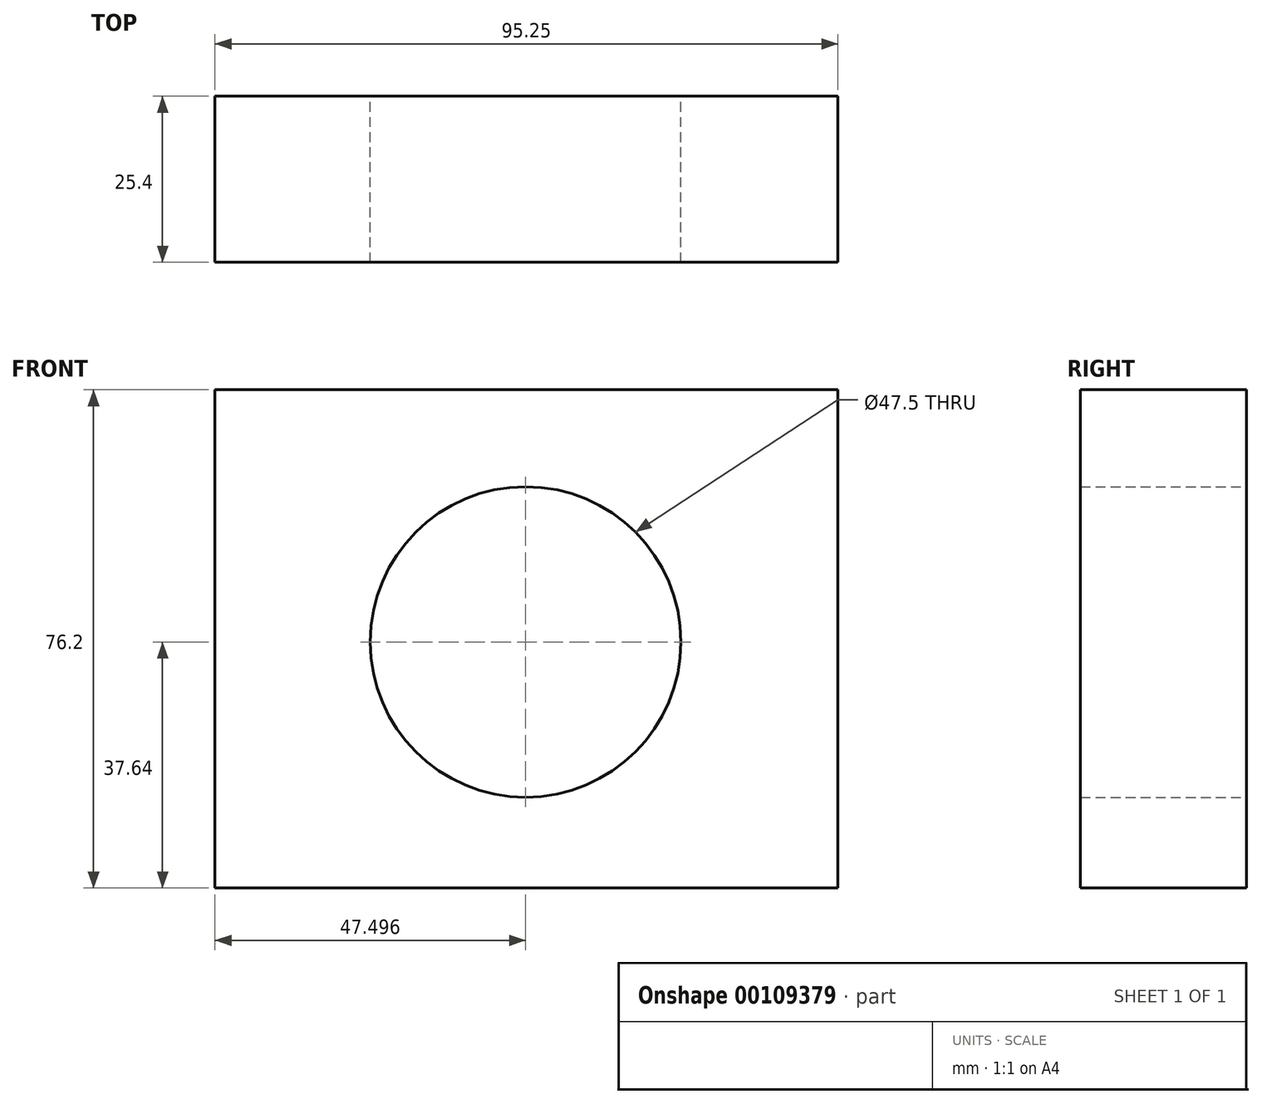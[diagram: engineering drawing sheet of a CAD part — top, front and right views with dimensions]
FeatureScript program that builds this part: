
annotation { "Feature Type Name" : "Feature", "Feature Type Description" : "" }
export const myFeature = defineFeature(function(context is Context, id is Id, definition is map)
    precondition{}
    {
        {
            var Q0;
            Q0=qCreatedBy(makeId("Front.planeOp"),FACE);
            var sketch = newSketch(context, id + "F0", { "sketchPlane" : qUnion([Q0])});
            skLineSegment(sketch, "E0", {"start": v(-36.86, 38.56) * mm, "end": v(-36.86, -37.64) * mm});
            skLineSegment(sketch, "E1", {"start": v(-36.86, -37.64) * mm, "end": v(58.39, -37.64) * mm});
            skLineSegment(sketch, "E2", {"start": v(58.39, -37.64) * mm, "end": v(58.39, 38.56) * mm});
            skLineSegment(sketch, "E3", {"start": v(58.39, 38.56) * mm, "end": v(-36.86, 38.56) * mm});
            skLineSegment(sketch, "E4", {"start": v(58.39, 0.46) * mm, "end": v(10.64, 0) * mm, "construction": true});
            skCircle(sketch, "E5", {"center": v(10.64, 0) * mm, "radius": 23.75 * mm});
            skSolve(sketch);
        }
        {
            var Q0;
            Q0=makeQuery(id+"F0.imprint","IMPRINT",FACE,{"disambiguationData":[TD([[makeQuery(id+"F0.imprint","IMPRINT",EDGE,{"derivedFrom":sQuery(id+"F0.wireOp",EDGE,"E0")}),1.0]])]});
            extrude(context, id + "F1", {"entities" : qUnion([Q0]), "depth" : 25.4 * mm});
        }
        {
            var Q0;
            Q0 = qSketchRegion(id + "F0", true);
            extrude(context, id + "F2", {"entities" : qUnion([Q0]), "operationType" : NewBodyOperationType.REMOVE, "oppositeDirection" : true, "depth" : 25.4 * mm});
        }
    });
